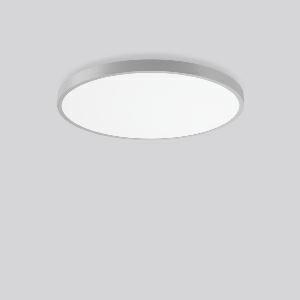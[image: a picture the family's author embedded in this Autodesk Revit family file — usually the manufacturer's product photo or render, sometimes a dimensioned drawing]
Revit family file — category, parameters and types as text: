
# Revit family: triona_round_a_312387_004_76_37f7
name_source: partatom
category: Lighting Fixtures
units: mm (PartAtom-declared; Revit-internal decimal feet)

## family parameters
Cut with Voids When Loaded = No
Host = Face
Light Source = No
Part Type = Normal
Room Calculation Point = No
Round Connector Dimension = Use Diameter
Shared = No

## types (1)
- TRIONA round A (1 x LED Modul 830, 8000 lm, 3000)
    Apparent Load = 80 VA
    CIE Flux Codes = 49 80 96 100 100
    Color Rendering = 80
    Color Temperature = 3000
    Default Elevation = 1800 mm
    Description = Series: TRIONA round
Decorative round LED surface-mounted luminaire. Flat, seamless frame: aluminium extrusion profile, powder coated. Cover made of sheet steel, powder-coated. Light emission through a diffuser: plastic, opal. Lightguide and diffuser made of non-yellowing plastic (PMMA). Lateral light emission (RZB SIDELITE technology) for above-average homogeneous light distribution. Suitable for Ceiling mounting, Wall (surface). Tool-free mounting via bayonet connection. Electronic ballast included. Very easy installation thanks to Plug+Play connection. 
Colour: silver, matt (approx. RAL 9006)
Diameter: 845 mm
Height: 88 mm
Lamp: LED
Socket: without socket
Colour temperature: 3000K
Colour rendering index (CRI): 80
System power: 80 W
Rated luminous flux: 8000 lm
Luminous efficiency: 100 lm/W
Control gear: Converter, dimmable, DALI
Protection class: I
Type of protection: IP 20
    Height = 88 mm
    Lamp = 1 x LED Modul 830
    Lamp Light Flux = 8000 lm
    Lamp count = 1
    Length = 845 mm
    Lifetime = 50000 h
    Luminous efficacy = 100 lm/W
    Manufacturer = RZB
    ModVariant = No
    Model = 312387.004.76
    Mounting Place = Ceiling
    Mounting Type = Surface mounted
    Number of Poles = 1
    OnlyDefault = Yes
    Power Factor = 1
    Product Name = TRIONA round A
    Product group = Surface mounted modular luminaires
    ProductGroupID = 306
    Protection Class = Protection class I
    Protection Degree = IP 20
    RLX_Detail_Level = 1
    RLX_Emergency_Light_Flux = 0 lm
    RLX_Emergency_Type = 0
    RLX_Emergency_Type_DB = No
    RlxData = <blob elided: 34125 chars, md5=f1bbd956>
    Socket = socket
    Standby Power = 0 W
    System Light Flux = 8000 lm
    System Power = 80 W
    Type Comments = Product without accessories
    Type Image = 312388.004.jpg
    URL = http://relux.com
    VarID = ---
    Voltage = 230 V
    Voltage Range = 220-240 V
    Weight = 0.00 kg
    Width = 0 mm  [stored 0 ft]

note: [stored X ft] marks values corroborated as IEEE doubles in the binary element streams (Revit-internal decimal feet)

## geometry (parser evidence)
native form markers: Blend x4, Sweep x9
no freeform markers — native parametric forms only
